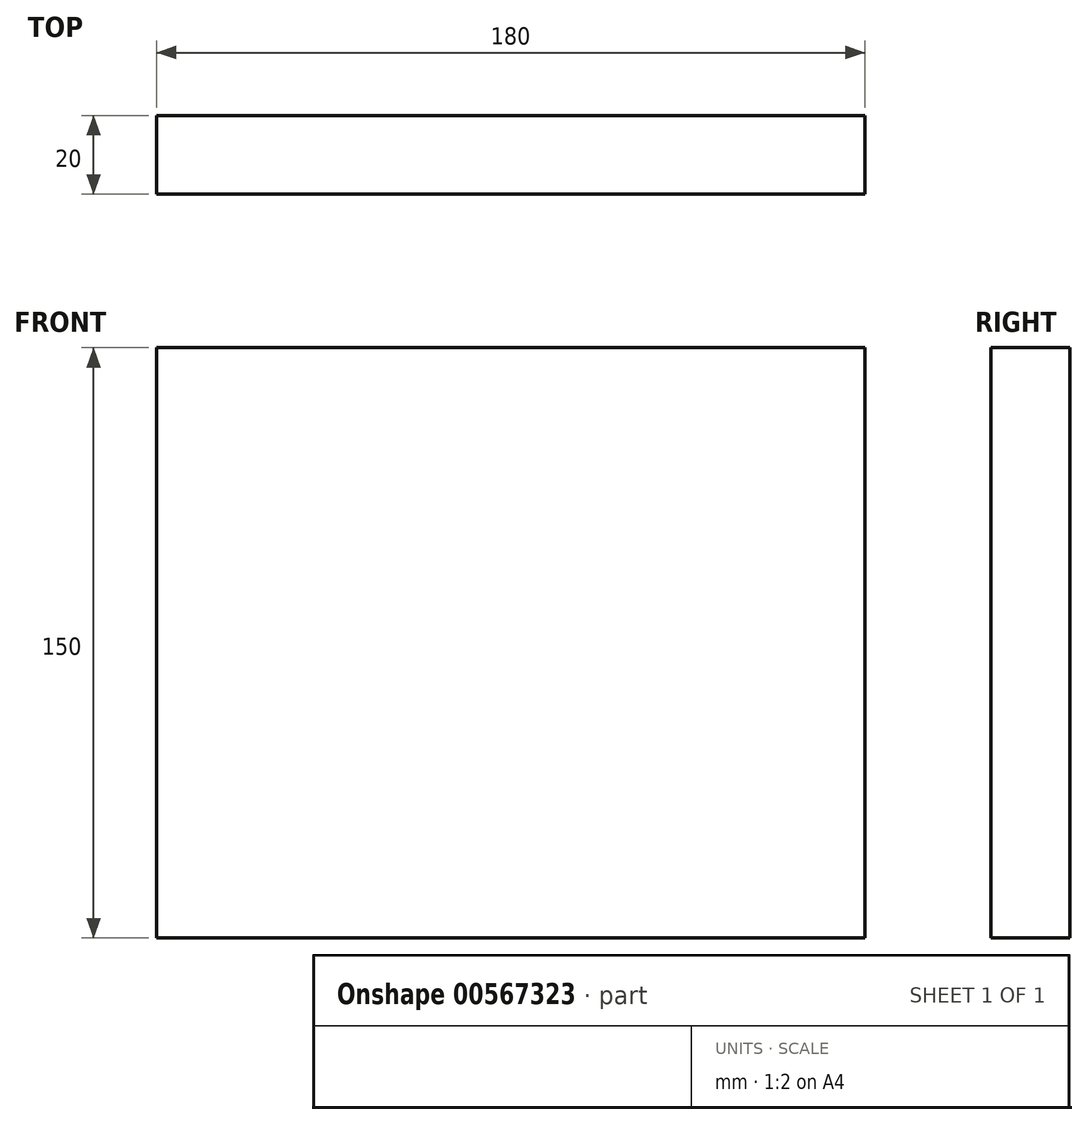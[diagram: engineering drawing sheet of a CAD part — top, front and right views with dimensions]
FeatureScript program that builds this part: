
annotation { "Feature Type Name" : "Feature", "Feature Type Description" : "" }
export const myFeature = defineFeature(function(context is Context, id is Id, definition is map)
    precondition{}
    {
        {
            var Q0;
            Q0=qCreatedBy(makeId("Front.planeOp"),FACE);
            var sketch = newSketch(context, id + "F0", { "sketchPlane" : qUnion([Q0])});
            skLineSegment(sketch, "E0.bottom", {"start": v(-102.1, 88.1) * mm, "end": v(77.9, 88.1) * mm});
            skLineSegment(sketch, "E0.top", {"start": v(-102.1, -61.9) * mm, "end": v(77.9, -61.9) * mm});
            skLineSegment(sketch, "E0.left", {"start": v(-102.1, 88.1) * mm, "end": v(-102.1, -61.9) * mm});
            skLineSegment(sketch, "E0.right", {"start": v(77.9, 88.1) * mm, "end": v(77.9, -61.9) * mm});
            skSolve(sketch);
        }
        {
            var Q0;
            Q0 = qSketchRegion(id + "F0", true);
            extrude(context, id + "F1", {"entities" : qUnion([Q0]), "depth" : 20 * mm, "offsetDistance" : 25.4 * mm});
        }
    });
